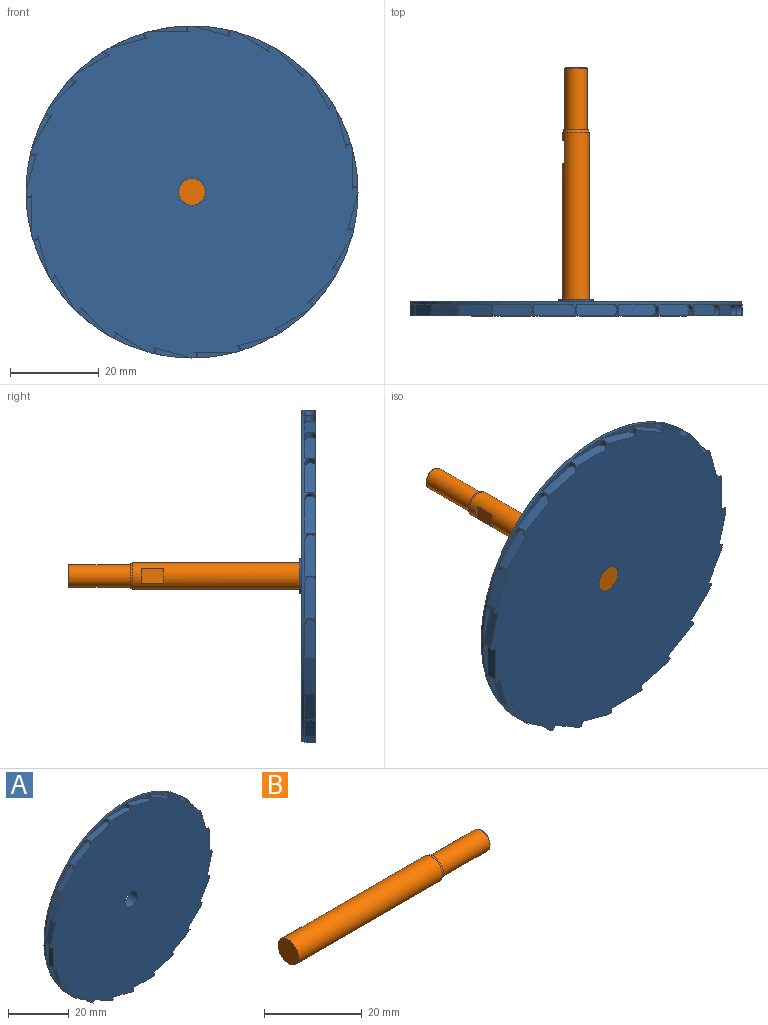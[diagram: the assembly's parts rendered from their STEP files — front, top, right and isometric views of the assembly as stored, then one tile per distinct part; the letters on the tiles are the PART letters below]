
ASSEMBLY  parts=2 mates=1
PART A: 78 faces, bbox 75x3.7x75 mm
  f0: cylinder r=1.25mm len=2.48mm, axis (0,0,-1), area 4.7mm2, adj f47,f48,f51,f77
  f1: cylinder r=1.25mm len=2.48mm, axis (-0.26,0,-0.97), area 4.7mm2, adj f46,f48,f52,f77
  f2: cylinder r=1.25mm len=2.48mm, axis (-0.5,0,-0.87), area 4.7mm2, adj f45,f48,f53,f77
  f3: cylinder r=1.25mm len=2.48mm, axis (-0.71,0,-0.71), area 4.7mm2, adj f44,f48,f54,f77
  f4: cylinder r=1.25mm len=2.48mm, axis (-0.87,0,-0.5), area 4.7mm2, adj f43,f48,f55,f77
  f5: cylinder r=1.25mm len=2.48mm, axis (-0.97,0,-0.26), area 4.7mm2, adj f42,f48,f56,f77
  f6: cylinder r=1.25mm len=2.48mm, axis (-1,0,0), area 4.7mm2, adj f41,f48,f57,f77
  f7: cylinder r=1.25mm len=2.48mm, axis (-0.97,0,0.26), area 4.7mm2, adj f40,f48,f58,f77
  f8: cylinder r=1.25mm len=2.48mm, axis (-0.87,0,0.5), area 4.7mm2, adj f39,f48,f59,f77
  f9: cylinder r=1.25mm len=2.48mm, axis (-0.71,0,0.71), area 4.7mm2, adj f38,f48,f60,f77
  f10: cylinder r=1.25mm len=2.48mm, axis (-0.5,0,0.87), area 4.7mm2, adj f37,f48,f61,f77
  f11: cylinder r=1.25mm len=2.48mm, axis (-0.26,0,0.97), area 4.7mm2, adj f36,f48,f62,f77
  f12: cylinder r=1.25mm len=2.48mm, axis (0,0,1), area 4.7mm2, adj f35,f48,f63,f77
  f13: cylinder r=1.25mm len=2.48mm, axis (0.26,0,0.97), area 4.7mm2, adj f34,f48,f64,f77
  f14: cylinder r=1.25mm len=2.48mm, axis (0.5,0,0.87), area 4.7mm2, adj f33,f48,f65,f77
  f15: cylinder r=1.25mm len=2.48mm, axis (0.71,0,0.71), area 4.7mm2, adj f32,f48,f66,f77
  f16: cylinder r=1.25mm len=2.48mm, axis (0.87,0,0.5), area 4.7mm2, adj f31,f48,f67,f77
  f17: cylinder r=1.25mm len=2.48mm, axis (0.97,0,0.26), area 4.7mm2, adj f30,f48,f68,f77
  f18: cylinder r=1.25mm len=2.48mm, axis (1,0,0), area 4.7mm2, adj f29,f48,f69,f77
  f19: cylinder r=1.25mm len=2.48mm, axis (0.97,0,-0.26), area 4.7mm2, adj f28,f48,f70,f77
  f20: cylinder r=1.25mm len=2.48mm, axis (0.87,0,-0.5), area 4.7mm2, adj f27,f48,f71,f77
  f21: cylinder r=1.25mm len=2.48mm, axis (0.71,0,-0.71), area 4.7mm2, adj f26,f48,f72,f77
  f22: cylinder r=1.25mm len=2.48mm, axis (0.5,0,-0.87), area 4.7mm2, adj f25,f48,f73,f77
  f23: cylinder r=1.25mm len=2.48mm, axis (0.26,0,-0.97), area 4.7mm2, adj f24,f48,f74,f77
  f24: plane 9.3x2.49mm, normal (-0.26,0,0.97), area 23.2mm2, adj f23,f48,f74,f77
  f25: plane 8.34x4.82mm, normal (-0.5,0,0.87), area 23.2mm2, adj f22,f48,f73,f77
  f26: plane 6.81x6.81mm, normal (-0.71,0,0.71), area 23.2mm2, adj f21,f48,f72,f77
  f27: plane 8.34x4.82mm, normal (-0.87,0,0.5), area 23.2mm2, adj f20,f48,f71,f77
  f28: plane 9.3x2.49mm, normal (-0.97,0,0.26), area 23.2mm2, adj f19,f48,f70,f77
  f29: plane 9.63x2.48mm, normal (-1,0,0), area 23.2mm2, adj f18,f48,f69,f77
  f30: plane 9.3x2.49mm, normal (-0.97,0,-0.26), area 23.2mm2, adj f17,f48,f68,f77
  f31: plane 8.34x4.82mm, normal (-0.87,0,-0.5), area 23.2mm2, adj f16,f48,f67,f77
  f32: plane 6.81x6.81mm, normal (-0.71,0,-0.71), area 23.2mm2, adj f15,f48,f66,f77
  f33: plane 8.34x4.82mm, normal (-0.5,0,-0.87), area 23.2mm2, adj f14,f48,f65,f77
  f34: plane 9.3x2.49mm, normal (-0.26,0,-0.97), area 23.2mm2, adj f13,f48,f64,f77
  f35: plane 9.63x2.48mm, normal (0,0,-1), area 23.2mm2, adj f12,f48,f63,f77
  f36: plane 9.3x2.49mm, normal (0.26,0,-0.97), area 23.2mm2, adj f11,f48,f62,f77
  f37: plane 8.34x4.82mm, normal (0.5,0,-0.87), area 23.2mm2, adj f10,f48,f61,f77
  f38: plane 6.81x6.81mm, normal (0.71,0,-0.71), area 23.2mm2, adj f9,f48,f60,f77
  f39: plane 8.34x4.82mm, normal (0.87,0,-0.5), area 23.2mm2, adj f8,f48,f59,f77
  f40: plane 9.3x2.49mm, normal (0.97,0,-0.26), area 23.2mm2, adj f7,f48,f58,f77
  f41: plane 9.63x2.48mm, normal (1,0,0), area 23.2mm2, adj f6,f48,f57,f77
  f42: plane 9.3x2.49mm, normal (0.97,0,0.26), area 23.2mm2, adj f5,f48,f56,f77
  f43: plane 8.34x4.82mm, normal (0.87,0,0.5), area 23.2mm2, adj f4,f48,f55,f77
  f44: plane 6.81x6.81mm, normal (0.71,0,0.71), area 23.2mm2, adj f3,f48,f54,f77
  f45: plane 8.34x4.82mm, normal (0.5,0,0.87), area 23.2mm2, adj f2,f48,f53,f77
  f46: plane 9.3x2.49mm, normal (0.26,0,0.97), area 23.2mm2, adj f1,f48,f52,f77
  f47: plane 9.63x2.48mm, normal (0,0,1), area 23.2mm2, adj f0,f48,f51,f77
  f48: cylinder r=37.5mm len=75mm, axis (0,-1,0), area 196.8mm2, adj f0,f1,f2,f3,f4,f5,f6,f7
  f49: cylinder r=3mm len=6mm, axis (0,-1,0), area 70.3mm2, adj f76,f77
  f50: plane 75x75mm, normal (0,1,0), area 4367.6mm2, adj f48,f75
  f51: plane 8.38x1.25mm, normal (0,-1,0), area 6.6mm2, adj f0,f47,f48
  f52: plane 8.42x2.17mm, normal (0,-1,0), area 6.6mm2, adj f1,f46,f48
  f53: plane 7.88x4.19mm, normal (0,-1,0), area 6.6mm2, adj f2,f45,f48
  f54: plane 6.81x5.93mm, normal (0,-1,0), area 6.6mm2, adj f3,f44,f48
  f55: plane 7.26x5.28mm, normal (0,-1,0), area 6.6mm2, adj f4,f43,f48
  f56: plane 8.09x3.38mm, normal (0,-1,0), area 6.6mm2, adj f5,f42,f48
  f57: plane 8.38x1.25mm, normal (0,-1,0), area 6.6mm2, adj f6,f41,f48
  f58: plane 8.42x2.17mm, normal (0,-1,0), area 6.6mm2, adj f7,f40,f48
  f59: plane 7.88x4.19mm, normal (0,-1,0), area 6.6mm2, adj f8,f39,f48
  f60: plane 6.81x5.93mm, normal (0,-1,0), area 6.6mm2, adj f9,f38,f48
  f61: plane 7.26x5.28mm, normal (0,-1,0), area 6.6mm2, adj f10,f37,f48
  f62: plane 8.09x3.38mm, normal (0,-1,0), area 6.6mm2, adj f11,f36,f48
  f63: plane 8.38x1.25mm, normal (0,-1,0), area 6.6mm2, adj f12,f35,f48
  f64: plane 8.42x2.17mm, normal (0,-1,0), area 6.6mm2, adj f13,f34,f48
  f65: plane 7.88x4.19mm, normal (0,-1,0), area 6.6mm2, adj f14,f33,f48
  f66: plane 6.81x5.93mm, normal (0,-1,0), area 6.6mm2, adj f15,f32,f48
  f67: plane 7.26x5.28mm, normal (0,-1,0), area 6.6mm2, adj f16,f31,f48
  f68: plane 8.09x3.38mm, normal (0,-1,0), area 6.6mm2, adj f17,f30,f48
  f69: plane 8.38x1.25mm, normal (0,-1,0), area 6.6mm2, adj f18,f29,f48
  f70: plane 8.42x2.17mm, normal (0,-1,0), area 6.6mm2, adj f19,f28,f48
  f71: plane 7.88x4.19mm, normal (0,-1,0), area 6.6mm2, adj f20,f27,f48
  f72: plane 6.81x5.93mm, normal (0,-1,0), area 6.6mm2, adj f21,f26,f48
  f73: plane 7.26x5.28mm, normal (0,-1,0), area 6.6mm2, adj f22,f25,f48
  f74: plane 8.09x3.38mm, normal (0,-1,0), area 6.6mm2, adj f23,f24,f48
  f75: cylinder r=4mm len=8mm, axis (0,-1,0), area 12.6mm2, adj f50,f76
  f76: plane 8x8mm, normal (0,1,0), area 22mm2, adj f49,f75
  f77: plane 75x75mm, normal (0,-1,0), area 4224.1mm2, adj f0,f1,f2,f3,f4,f5,f6,f7
PART B: 10 faces, bbox 56x6x6 mm
  f0: plane 5.73x5.73mm, normal (1,0,0), area 6.1mm2, adj f1,f7
  f1: cone r=3mm half-angle=15deg, axis (-1,0,0), area 9.5mm2, adj f0,f2
  f2: cylinder r=3mm len=41.49mm, axis (1,0,0), area 763.7mm2, adj f1,f3,f4,f5,f6
  f3: plane 5.99x5.99mm, normal (-1,0,0), area 28.2mm2, adj f2
  f4: plane 3.3x0.5mm, normal (1,0,0), area 1.1mm2, adj f2,f6
  f5: plane 3.3x0.5mm, normal (-1,0,0), area 1.1mm2, adj f2,f6
  f6: plane 5x3.3mm, normal (0,1,0), area 16.5mm2, adj f2,f4,f5
  f7: cylinder r=2.5mm len=13.8mm, axis (-1,0,0), area 216.8mm2, adj f0,f9
  f8: plane 4.6x4.6mm, normal (1,0,0), area 16.6mm2, adj f9
  f9: cone r=2.3mm half-angle=45deg, axis (-1,0,0), area 4.3mm2, adj f7,f8
PLACE A t=(0,-0.77,0)mm
PLACE B rot(axis=(0,0,1),90deg) t=(0,0,0)mm
MATE fastened B.f1 <-> A.f49  axis (0,-1,0) through (0,0,0)mm
